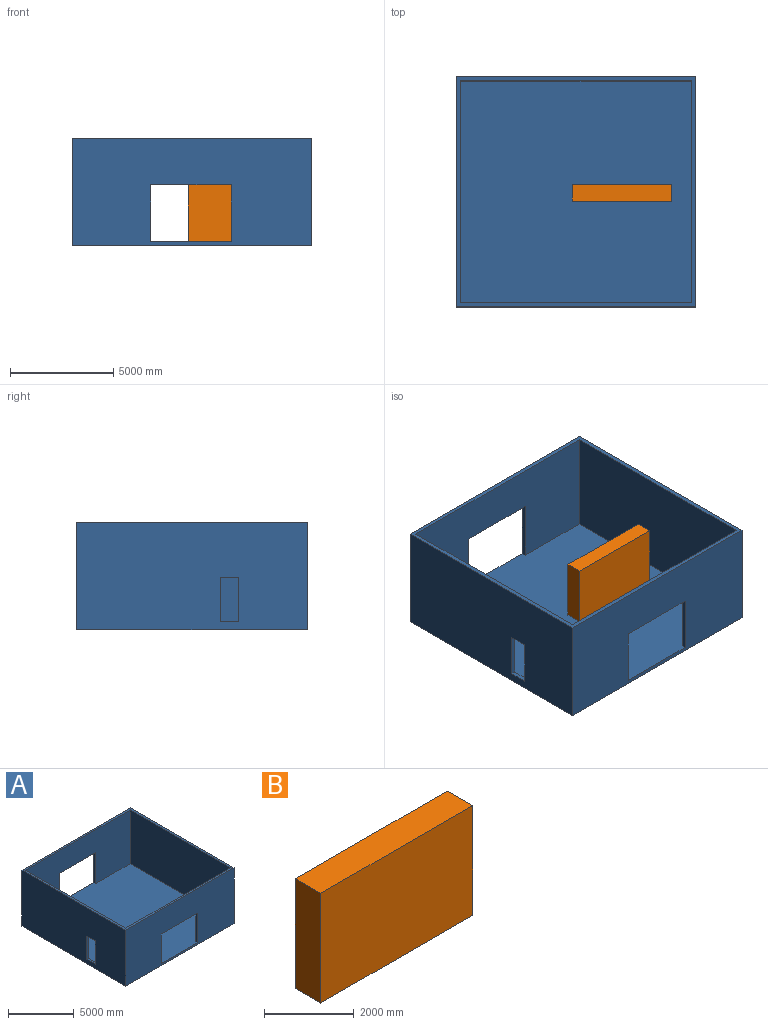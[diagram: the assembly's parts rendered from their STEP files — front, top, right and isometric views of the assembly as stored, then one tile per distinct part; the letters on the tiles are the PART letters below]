
ASSEMBLY  parts=2 mates=2
PART A: 21 faces, bbox 11600x11150x5200 mm
  f0: plane 2750x200mm, normal (-1,0,0), area 550000mm2, adj f2,f7,f9,f20
  f1: plane 2900x200mm, normal (-1,0,0), area 580000mm2, adj f4,f5,f17,f20
  f2: plane 11600x5200mm, normal (0,-1,0), area 49595000mm2, adj f0,f3,f8,f9,f11,f14,f19,f20
  f3: plane 11150x5200mm, normal (1,0,0), area 57980000mm2, adj f2,f4,f8,f19
  f4: plane 11600x5200mm, normal (0,1,0), area 49010000mm2, adj f1,f3,f8,f11,f16,f17,f19,f20
  f5: plane 11200x5000mm, normal (0,-1,0), area 44690000mm2, adj f1,f6,f8,f10,f16,f17,f20
  f6: plane 10750x5000mm, normal (-1,0,0), area 53750000mm2, adj f5,f7,f8,f20
  f7: plane 11200x5000mm, normal (0,1,0), area 45275000mm2, adj f0,f6,f8,f9,f10,f14,f20
  f8: plane 11600x11150mm, normal (0,0,1), area 8940000mm2, adj f2,f3,f4,f5,f6,f7,f10,f11
  f9: plane 3900x200mm, normal (0,0,-1), area 780000mm2, adj f0,f2,f7,f14
  f10: plane 10750x5000mm, normal (1,0,0), area 51858000mm2, adj f5,f7,f8,f12,f13,f15,f18,f20
  f11: plane 11150x5200mm, normal (-1,0,0), area 56088000mm2, adj f2,f4,f8,f12,f13,f15,f18,f19
  f12: plane 880x200mm, normal (0,0,-1), area 176000mm2, adj f10,f11,f13,f15
  f13: plane 2150x200mm, normal (0,1,0), area 430000mm2, adj f10,f11,f12,f18
  f14: plane 2750x200mm, normal (1,0,0), area 550000mm2, adj f2,f7,f9,f20
  f15: plane 2150x200mm, normal (0,-1,0), area 430000mm2, adj f10,f11,f12,f18
  f16: plane 2900x200mm, normal (1,0,0), area 580000mm2, adj f4,f5,f17,f20
  f17: plane 3900x200mm, normal (0,0,-1), area 780000mm2, adj f1,f4,f5,f16
  f18: plane 880x200mm, normal (0,0,1), area 176000mm2, adj f10,f11,f13,f15
  f19: plane 11600x11150mm, normal (0,0,-1), area 129340000mm2, adj f2,f3,f4,f11
  f20: plane 11200x11150mm, normal (0,0,1), area 121960000mm2, adj f0,f1,f2,f4,f5,f6,f7,f10
PART B: 6 faces, bbox 4800x800x3000 mm
  f0: plane 3000x800mm, normal (-1,0,0), area 2400000mm2, adj f1,f3,f4,f5
  f1: plane 4800x3000mm, normal (0,-1,0), area 14400000mm2, adj f0,f2,f4,f5
  f2: plane 3000x800mm, normal (1,0,0), area 2400000mm2, adj f1,f3,f4,f5
  f3: plane 4800x3000mm, normal (0,1,0), area 14400000mm2, adj f0,f2,f4,f5
  f4: plane 4800x800mm, normal (0,0,1), area 3840000mm2, adj f0,f1,f2,f3
  f5: plane 4800x800mm, normal (0,0,-1), area 3840000mm2, adj f0,f1,f2,f3
PLACE A t=(413.24,-9745.93,-918.61)mm
PLACE B t=(223.11,-10187.34,-918.61)mm
MATE parallel B.f3 <-> B.f3  axis (0,1,0) through (2623.11,-9387.34,581.39)mm
MATE planar B.f5 <-> A.f20  axis (0,0,-1) through (2623.11,-9787.34,-918.61)mm
